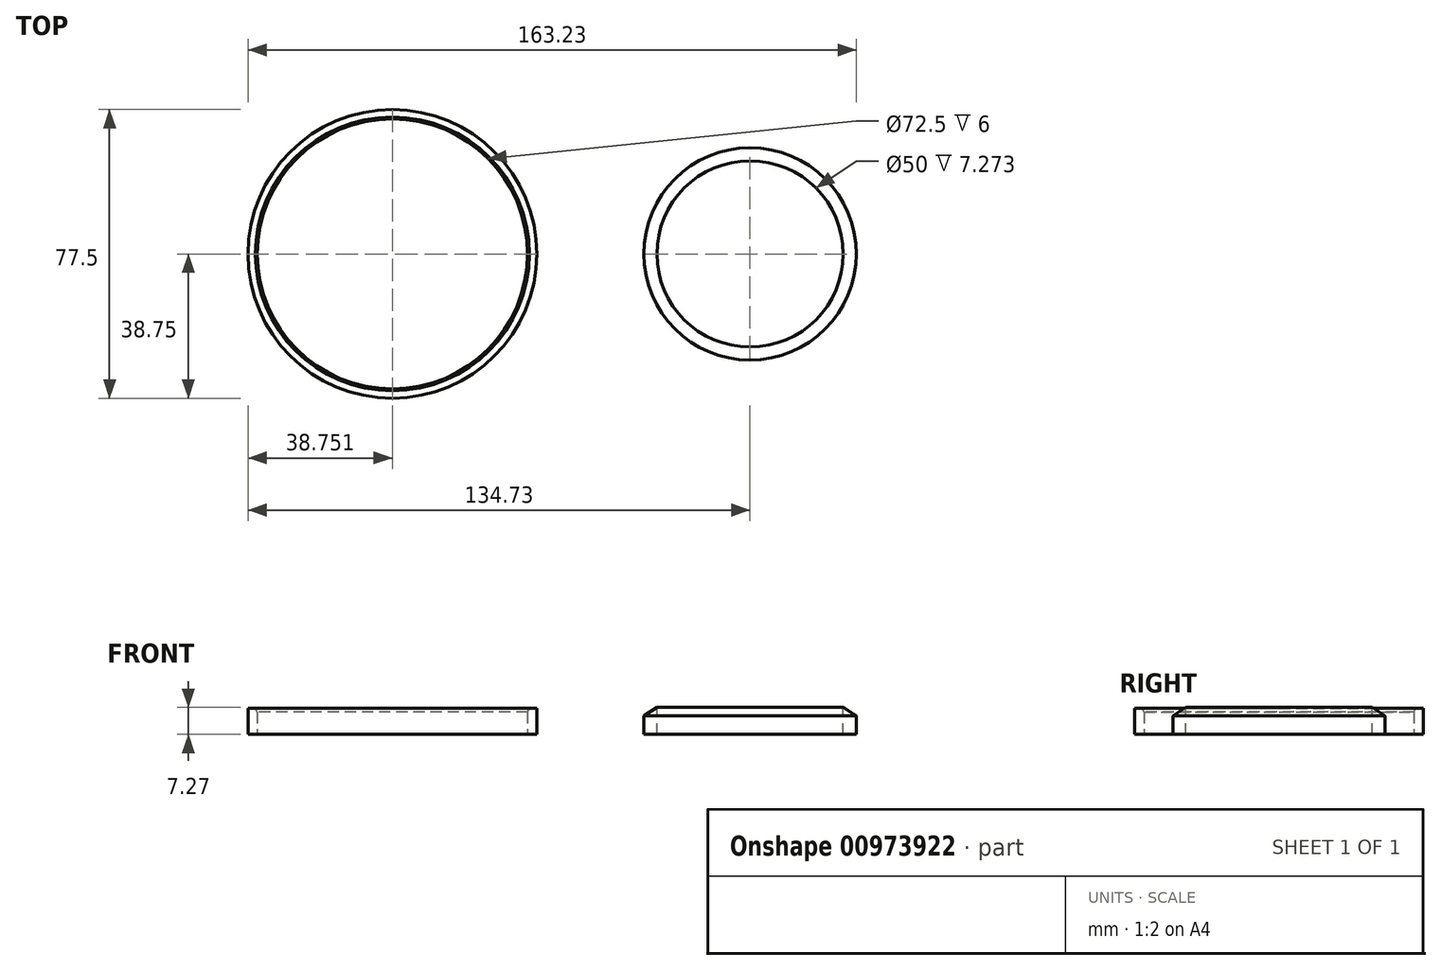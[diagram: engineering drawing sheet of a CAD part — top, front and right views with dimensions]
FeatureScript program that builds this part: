
annotation { "Feature Type Name" : "Feature", "Feature Type Description" : "" }
export const myFeature = defineFeature(function(context is Context, id is Id, definition is map)
    precondition{}
    {
        {
            var Q0;
            Q0=qCreatedBy(makeId("Front.planeOp"),FACE);
            var sketch = newSketch(context, id + "F0", { "sketchPlane" : qUnion([Q0])});
            skLineSegment(sketch, "E0", {"start": v(0, 0) * mm, "end": v(0, -33.83) * mm});
            skLineSegment(sketch, "E1", {"start": v(-25, 0) * mm, "end": v(-28.5, 0) * mm});
            skLineSegment(sketch, "E2", {"start": v(-28.5, 0) * mm, "end": v(-28.5, 5) * mm});
            skLineSegment(sketch, "E3", {"start": v(-28.5, 5) * mm, "end": v(-25, 7.27) * mm});
            skLineSegment(sketch, "E4", {"start": v(-25, 7.27) * mm, "end": v(-25, 0) * mm});
            skSolve(sketch);
        }
        {
            var Q0;
            Q0=makeQuery(id+"F0.imprint","IMPRINT",FACE,{"disambiguationData":[TD([[makeQuery(id+"F0.imprint","IMPRINT",EDGE,{"derivedFrom":sQuery(id+"F0.wireOp",EDGE,"E1")}),-1.0]])]});
            var Q1;
            Q1=sQuery(id+"F0.wireOp",EDGE,"E0");
            revolve(context, id + "F1", {"surfaceOperationType" : NewSurfaceOperationType.NEW, "entities" : qUnion([Q0]), "axis" : qUnion([Q1]), "revolveType" : RevolveType.FULL});
        }
        {
            var Q0;
            Q0=qCreatedBy(makeId("Top.planeOp"),FACE);
            var sketch = newSketch(context, id + "F2", { "sketchPlane" : qUnion([Q0])});
            skCircle(sketch, "E5", {"center": v(-95.98, 0) * mm, "radius": 36.25 * mm});
            skCircle(sketch, "E6", {"center": v(-95.98, 0) * mm, "radius": 38.75 * mm});
            skSolve(sketch);
        }
        {
            var Q0;
            Q0=makeQuery(id+"F2.imprint","IMPRINT",FACE,{"disambiguationData":[TD([[makeQuery(id+"F2.imprint","IMPRINT",EDGE,{"derivedFrom":sQuery(id+"F2.wireOp",EDGE,"E5")}),-1.0]])]});
            extrude(context, id + "F3", {"entities" : qUnion([Q0]), "depth" : 7 * mm, "offsetDistance" : 25 * mm});
        }
        {
            var Q0;
            Q0=makeQuery(id+"F3.opExtrude","CAP_EDGE",EDGE,{"disambiguationData":[OSD([sQuery(id+"F2.wireOp",EDGE,"E5")])],"isStart":false});
            chamfer(context, id + "F4", {"entities" : qUnion([Q0]), "chamferType" : ChamferType.TWO_OFFSETS, "width1" : 1 * mm, "oppositeDirection" : false, "width2" : 0.5 * mm, "tangentPropagation" : true});
        }
    });
